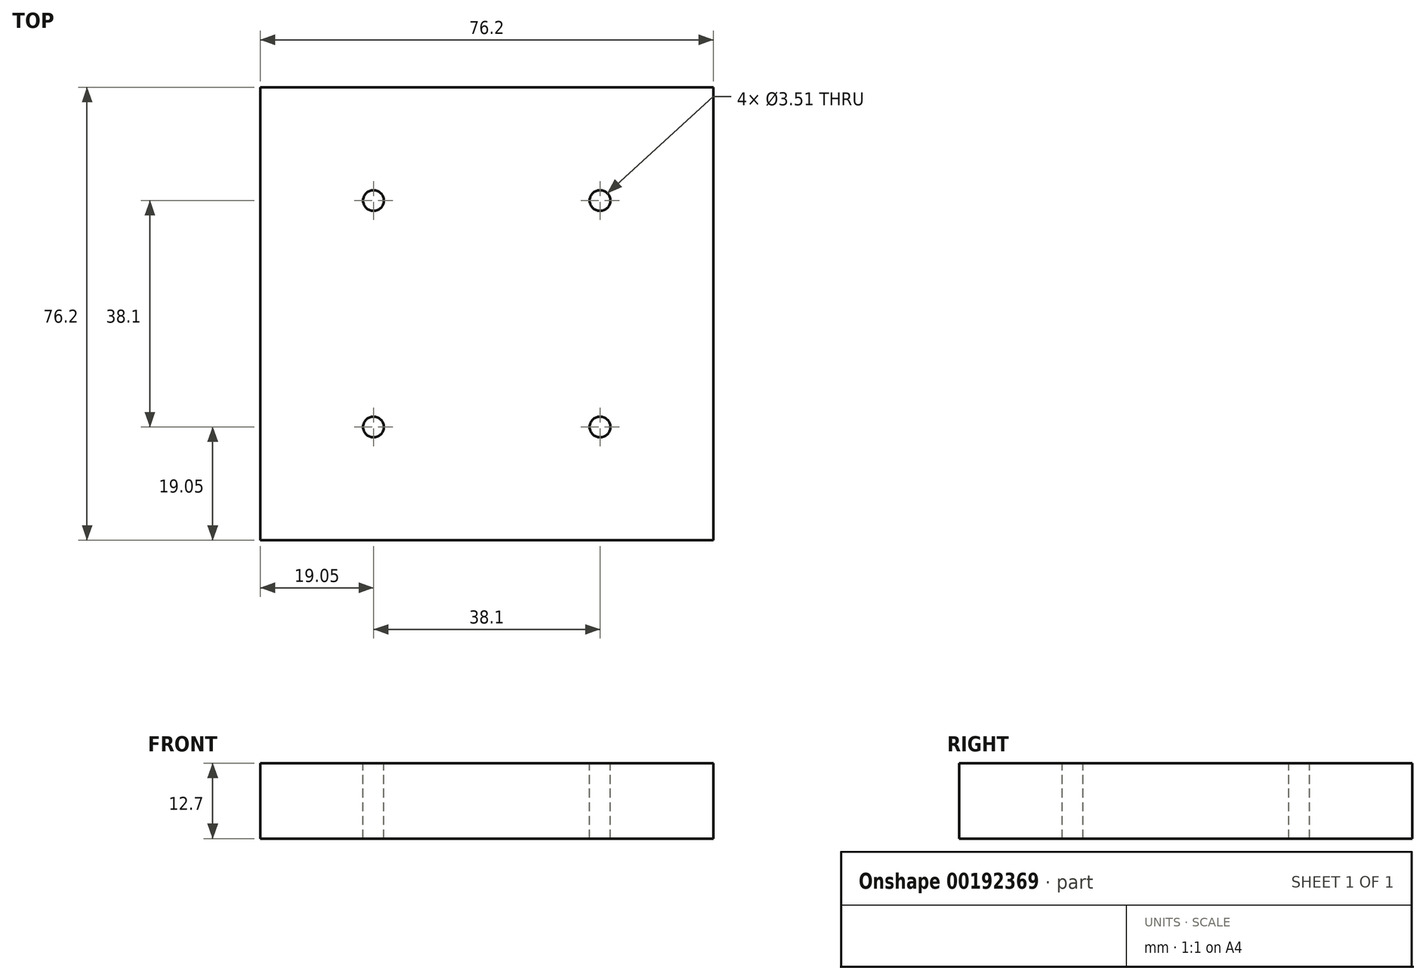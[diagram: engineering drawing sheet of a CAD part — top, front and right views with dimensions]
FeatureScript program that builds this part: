
annotation { "Feature Type Name" : "Feature", "Feature Type Description" : "" }
export const myFeature = defineFeature(function(context is Context, id is Id, definition is map)
    precondition{}
    {
        {
            var Q0;
            Q0=qCreatedBy(makeId("Top.planeOp"),FACE);
            var sketch = newSketch(context, id + "F0", { "sketchPlane" : qUnion([Q0])});
            skLineSegment(sketch, "E0.bottom", {"start": v(38.1, 38.1) * mm, "end": v(-38.1, 38.1) * mm});
            skLineSegment(sketch, "E0.top", {"start": v(38.1, -38.1) * mm, "end": v(-38.1, -38.1) * mm});
            skLineSegment(sketch, "E0.left", {"start": v(38.1, 38.1) * mm, "end": v(38.1, -38.1) * mm});
            skLineSegment(sketch, "E0.right", {"start": v(-38.1, 38.1) * mm, "end": v(-38.1, -38.1) * mm});
            skPoint(sketch, "E0.middle", {"position": v(0, 0) * mm});
            skSolve(sketch);
        }
        {
            var Q0;
            Q0=makeQuery(id+"F0.imprint","IMPRINT",FACE,{"disambiguationData":[TD([[makeQuery(id+"F0.imprint","IMPRINT",EDGE,{"derivedFrom":sQuery(id+"F0.wireOp",EDGE,"E0.bottom")}),1.0]])]});
            extrude(context, id + "F1", {"entities" : qUnion([Q0]), "depth" : 12.7 * mm});
        }
        {
            var Q0;
            Q0=makeQuery(id+"F1.opExtrude","CAP_FACE",FACE,{"disambiguationData":[OSD([sQuery(id+"F0.wireOp",EDGE,"E0.bottom"),sQuery(id+"F0.wireOp",EDGE,"E0.top"),sQuery(id+"F0.wireOp",EDGE,"E0.left"),sQuery(id+"F0.wireOp",EDGE,"E0.right")])],"isStart":false});
            var sketch = newSketch(context, id + "F2", { "sketchPlane" : qUnion([Q0])});
            skLineSegment(sketch, "E1.bottom", {"start": v(-38.1, 38.1) * mm, "end": v(-19.05, 38.1) * mm});
            skLineSegment(sketch, "E1.top", {"start": v(-38.1, 19.05) * mm, "end": v(-19.05, 19.05) * mm});
            skLineSegment(sketch, "E1.left", {"start": v(-38.1, 38.1) * mm, "end": v(-38.1, 19.05) * mm});
            skLineSegment(sketch, "E1.right", {"start": v(-19.05, 38.1) * mm, "end": v(-19.05, 19.05) * mm});
            skLineSegment(sketch, "E2.bottom", {"start": v(38.1, 38.1) * mm, "end": v(19.05, 38.1) * mm});
            skLineSegment(sketch, "E2.top", {"start": v(38.1, 19.05) * mm, "end": v(19.05, 19.05) * mm});
            skLineSegment(sketch, "E2.left", {"start": v(38.1, 38.1) * mm, "end": v(38.1, 19.05) * mm});
            skLineSegment(sketch, "E2.right", {"start": v(19.05, 38.1) * mm, "end": v(19.05, 19.05) * mm});
            skLineSegment(sketch, "E3.bottom", {"start": v(38.1, -38.1) * mm, "end": v(19.05, -38.1) * mm});
            skLineSegment(sketch, "E3.top", {"start": v(38.1, -19.05) * mm, "end": v(19.05, -19.05) * mm});
            skLineSegment(sketch, "E3.left", {"start": v(38.1, -38.1) * mm, "end": v(38.1, -19.05) * mm});
            skLineSegment(sketch, "E3.right", {"start": v(19.05, -38.1) * mm, "end": v(19.05, -19.05) * mm});
            skLineSegment(sketch, "E4.bottom", {"start": v(-38.1, -38.1) * mm, "end": v(-19.05, -38.1) * mm});
            skLineSegment(sketch, "E4.top", {"start": v(-38.1, -19.05) * mm, "end": v(-19.05, -19.05) * mm});
            skLineSegment(sketch, "E4.left", {"start": v(-38.1, -38.1) * mm, "end": v(-38.1, -19.05) * mm});
            skLineSegment(sketch, "E4.right", {"start": v(-19.05, -38.1) * mm, "end": v(-19.05, -19.05) * mm});
            skPoint(sketch, "E5", {"position": v(-19.05, 19.05) * mm});
            skPoint(sketch, "E6", {"position": v(-19.05, -19.05) * mm});
            skPoint(sketch, "E7", {"position": v(19.05, -19.05) * mm});
            skPoint(sketch, "E8", {"position": v(19.05, 19.05) * mm});
            skSolve(sketch);
        }
        {
            var Q0;
            Q0=sQuery(id+"F2.wireOp",VERTEX,"E5");
            var Q1;
            Q1=sQuery(id+"F2.wireOp",VERTEX,"E6");
            var Q2;
            Q2=sQuery(id+"F2.wireOp",VERTEX,"E7");
            var Q3;
            Q3=sQuery(id+"F2.wireOp",VERTEX,"E8");
            var Q4;
            Q4=makeQuery(id+"F1.opExtrude","SWEPT_BODY",BODY,{"disambiguationData":[OSD([sQuery(id+"F0.wireOp",EDGE,"E0.bottom"),sQuery(id+"F0.wireOp",EDGE,"E0.top"),sQuery(id+"F0.wireOp",EDGE,"E0.left"),sQuery(id+"F0.wireOp",EDGE,"E0.right")])]});
            hole(context, id + "F3", {"style" : HoleStyle.SIMPLE, "endStyle" : HoleEndStyle.THROUGH, "holeDiameter" : 3.5 * mm, "locations" : qUnion([Q0, Q1, Q2, Q3]), "scope" : qUnion([Q4]), "isTappedThrough" : true});
        }
    });
